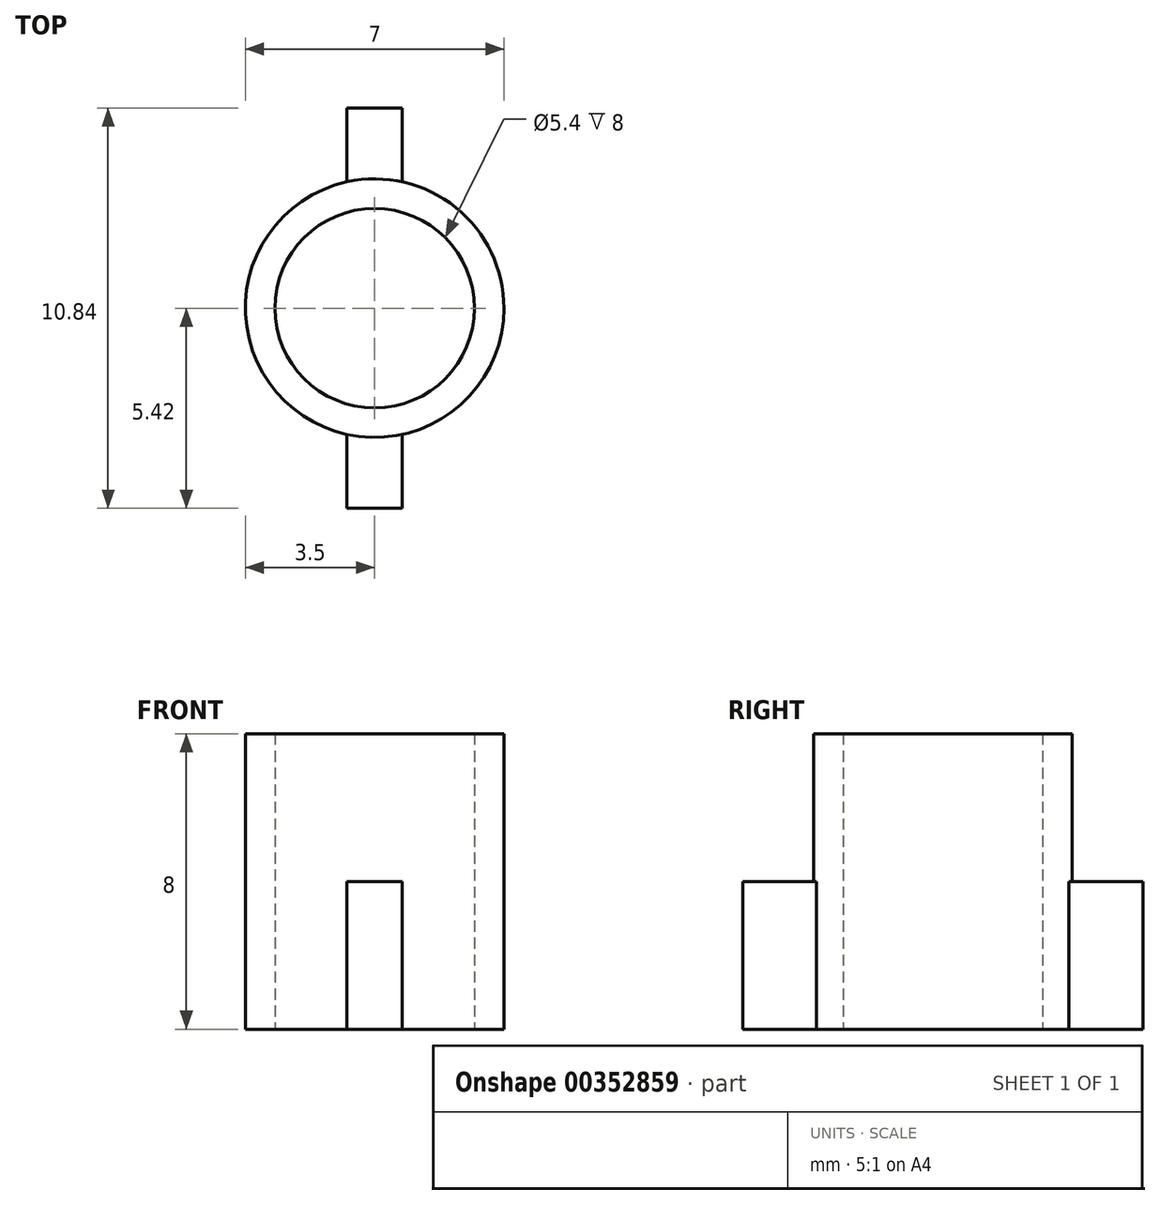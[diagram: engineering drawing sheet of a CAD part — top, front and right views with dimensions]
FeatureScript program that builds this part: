
annotation { "Feature Type Name" : "Feature", "Feature Type Description" : "" }
export const myFeature = defineFeature(function(context is Context, id is Id, definition is map)
    precondition{}
    {
        {
            var Q0;
            Q0=qCreatedBy(makeId("Top.planeOp"),FACE);
            var sketch = newSketch(context, id + "F0", { "sketchPlane" : qUnion([Q0])});
            skCircle(sketch, "E0", {"center": v(0, 0) * mm, "radius": 3.5 * mm});
            skCircle(sketch, "E1", {"center": v(0, 0) * mm, "radius": 2.7 * mm});
            skSolve(sketch);
        }
        {
            var Q0;
            Q0=makeQuery(id+"F0.imprint","IMPRINT",FACE,{"disambiguationData":[TD([[makeQuery(id+"F0.imprint","IMPRINT",EDGE,{"derivedFrom":sQuery(id+"F0.wireOp",EDGE,"E0")}),1.0]])]});
            extrude(context, id + "F1", {"entities" : qUnion([Q0]), "depth" : 8 * mm});
        }
        {
            var Q0;
            Q0=makeQuery(id+"F1.opExtrude","CAP_FACE",FACE,{"disambiguationData":[OSD([sQuery(id+"F0.wireOp",EDGE,"E0"),sQuery(id+"F0.wireOp",EDGE,"E1")])],"isStart":false});
            cPlane(context, id + "F2", {"entities" : qUnion([Q0]), "cplaneType" : CPlaneType.OFFSET, "offset" : 4 * mm, "oppositeDirection" : true, "width" : 150 * mm, "height" : 150 * mm});
        }
        {
            var Q0;
            Q0=qCreatedBy(id+"F2.planeOp",FACE);
            var sketch = newSketch(context, id + "F3", { "sketchPlane" : qUnion([Q0])});
            skLineSegment(sketch, "E2.bottom", {"start": v(-0.75, 5.42) * mm, "end": v(0.75, 5.42) * mm});
            skLineSegment(sketch, "E2.top", {"start": v(-0.75, 3.42) * mm, "end": v(0.75, 3.42) * mm});
            skLineSegment(sketch, "E2.left", {"start": v(-0.75, 5.42) * mm, "end": v(-0.75, 3.42) * mm});
            skLineSegment(sketch, "E2.right", {"start": v(0.75, 5.42) * mm, "end": v(0.75, 3.42) * mm});
            skLineSegment(sketch, "E3.bottom", {"start": v(-0.75, -3.42) * mm, "end": v(0.75, -3.42) * mm});
            skLineSegment(sketch, "E3.top", {"start": v(-0.75, -5.42) * mm, "end": v(0.75, -5.42) * mm});
            skLineSegment(sketch, "E3.left", {"start": v(-0.75, -3.42) * mm, "end": v(-0.75, -5.42) * mm});
            skLineSegment(sketch, "E3.right", {"start": v(0.75, -3.42) * mm, "end": v(0.75, -5.42) * mm});
            skSolve(sketch);
        }
        {
            var Q0;
            Q0=makeQuery(id+"F3.imprint","IMPRINT",FACE,{"disambiguationData":[TD([[makeQuery(id+"F3.imprint","IMPRINT",EDGE,{"derivedFrom":sQuery(id+"F3.wireOp",EDGE,"E2.bottom")}),-1.0]])]});
            var Q1;
            Q1=makeQuery(id+"F3.imprint","IMPRINT",FACE,{"disambiguationData":[TD([[makeQuery(id+"F3.imprint","IMPRINT",EDGE,{"derivedFrom":sQuery(id+"F3.wireOp",EDGE,"E3.bottom")}),-1.0]])]});
            var Q2;
            Q2=makeQuery(id+"F1.opExtrude","CAP_FACE",FACE,{"disambiguationData":[OSD([sQuery(id+"F0.wireOp",EDGE,"E0"),sQuery(id+"F0.wireOp",EDGE,"E1")])],"isStart":true});
            extrude(context, id + "F4", {"entities" : qUnion([Q0, Q1]), "operationType" : NewBodyOperationType.ADD, "endBound" : BoundingType.UP_TO_SURFACE, "oppositeDirection" : true, "endBoundEntityFace" : qUnion([Q2]), "depth" : 25 * mm});
        }
    });
